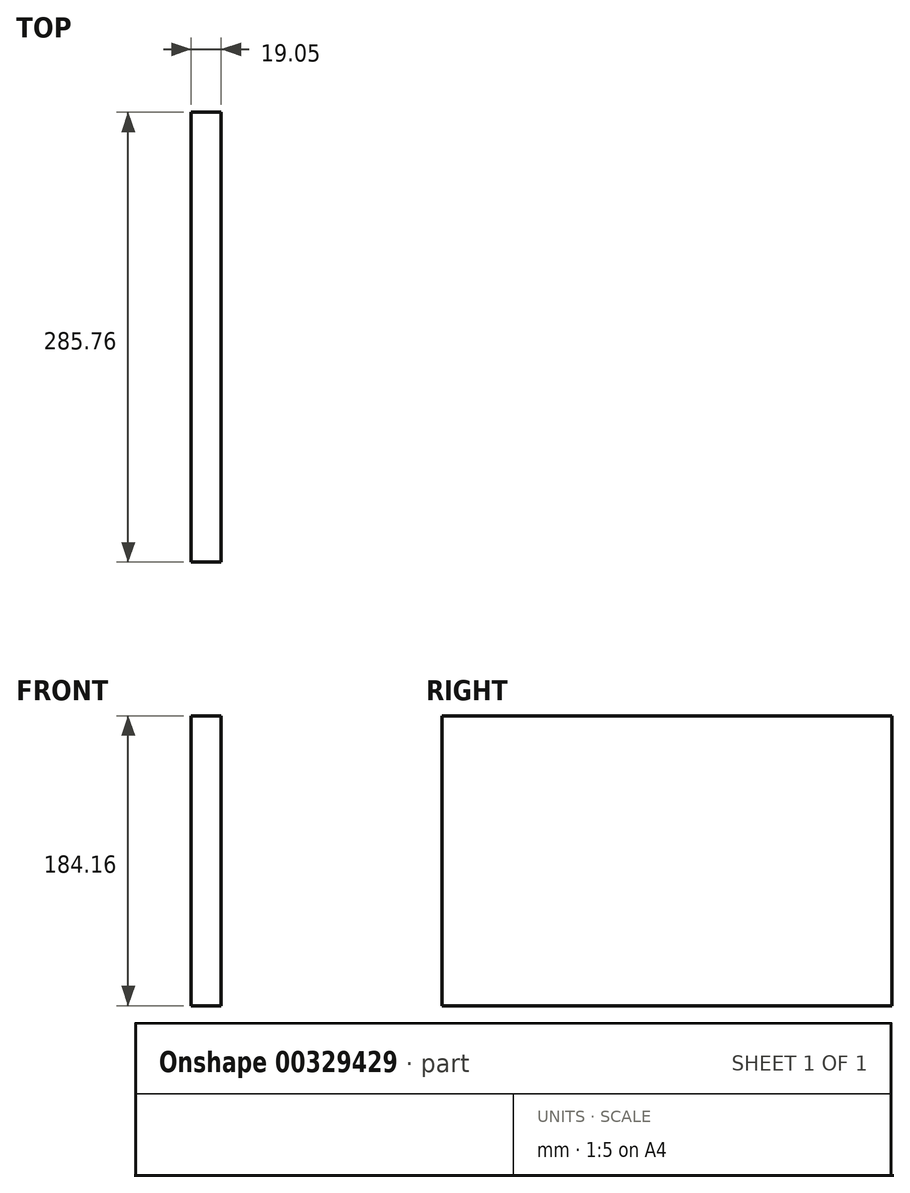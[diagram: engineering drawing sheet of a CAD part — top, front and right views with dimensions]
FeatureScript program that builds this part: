
annotation { "Feature Type Name" : "Feature", "Feature Type Description" : "" }
export const myFeature = defineFeature(function(context is Context, id is Id, definition is map)
    precondition{}
    {
        {
            var Q0;
            Q0=qCreatedBy(makeId("Right.planeOp"),FACE);
            var sketch = newSketch(context, id + "F0", { "sketchPlane" : qUnion([Q0])});
            skLineSegment(sketch, "E0.bottom", {"start": v(-142.88, 92.08) * mm, "end": v(142.88, 92.08) * mm});
            skLineSegment(sketch, "E0.top", {"start": v(-142.88, -92.08) * mm, "end": v(142.88, -92.08) * mm});
            skLineSegment(sketch, "E0.left", {"start": v(-142.88, 92.08) * mm, "end": v(-142.88, -92.08) * mm});
            skLineSegment(sketch, "E0.right", {"start": v(142.88, 92.08) * mm, "end": v(142.88, -92.08) * mm});
            skPoint(sketch, "E0.middle", {"position": v(0, 0) * mm});
            skSolve(sketch);
        }
        {
            var Q0;
            Q0=qSketchRegion(id+"F0",true);
            extrude(context, id + "F1", {"entities" : qUnion([Q0]), "depth" : 19.05 * mm});
        }
    });
